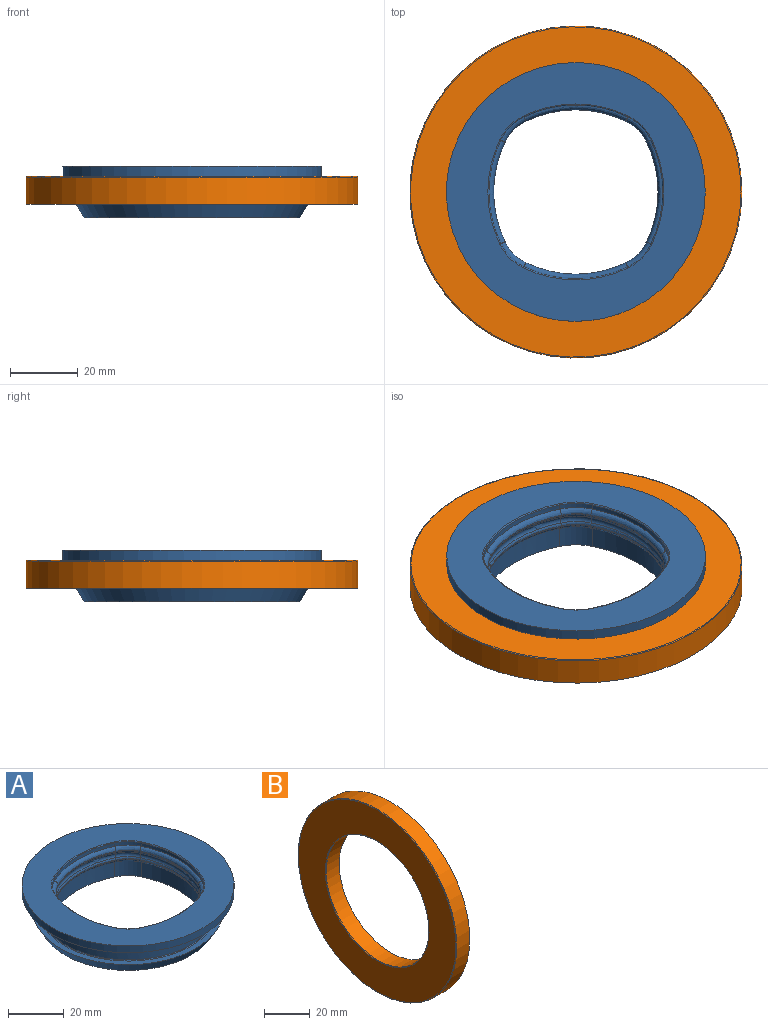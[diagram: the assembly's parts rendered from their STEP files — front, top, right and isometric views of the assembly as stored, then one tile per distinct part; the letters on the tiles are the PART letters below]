
ASSEMBLY  parts=2 mates=1
PART A: 89 faces, bbox 76.2x76.2x15.2 mm
  f0: cylinder r=38.1mm len=76.2mm, axis (0,0,1), area 717.5mm2, adj f2,f75
  f1: plane 63.5x63.5mm, normal (0,0,-1), area 997.1mm2, adj f19,f20,f21,f22,f23,f24,f25,f26
  f2: plane 76.2x76.2mm, normal (0,0,1), area 2340.6mm2, adj f0,f81,f82,f83,f84,f85,f86,f87
  f3: cylinder r=14.09mm len=6.8mm, axis (0,0,-1), area 14.5mm2, adj f4,f5,f16,f88
  f4: cylinder r=34.92mm len=30.56mm, axis (0,0,-1), area 46.7mm2, adj f3,f6,f17,f86
  f5: cylinder r=34.92mm len=30.56mm, axis (0,0,-1), area 46.7mm2, adj f3,f7,f15,f87
  f6: cylinder r=14.09mm len=6.8mm, axis (0,0,-1), area 14.5mm2, adj f4,f8,f18,f84
  f7: cylinder r=14.09mm len=6.8mm, axis (0,0,-1), area 14.5mm2, adj f5,f9,f14,f85
  f8: cylinder r=34.92mm len=30.56mm, axis (0,0,-1), area 46.7mm2, adj f6,f10,f11,f82
  f9: cylinder r=34.92mm len=30.56mm, axis (0,0,-1), area 46.7mm2, adj f7,f10,f13,f83
  f10: cylinder r=14.09mm len=6.8mm, axis (0,0,-1), area 14.5mm2, adj f8,f9,f12,f81
  f11: bspline ~30.7x5.32mm, area 63.4mm2, adj f8,f12,f18,f35
  f12: bspline ~7.41x7.41mm, area 19mm2, adj f10,f11,f13,f36
  f13: bspline ~30.7x5.32mm, area 63.4mm2, adj f9,f12,f14,f37
  f14: bspline ~7.41x7.41mm, area 19mm2, adj f7,f13,f15,f38
  f15: bspline ~30.7x5.32mm, area 63.4mm2, adj f5,f14,f16,f39
  f16: bspline ~7.41x7.41mm, area 19mm2, adj f3,f15,f17,f40
  f17: bspline ~30.7x5.32mm, area 63.4mm2, adj f4,f16,f18,f41
  f18: bspline ~7.41x7.41mm, area 19mm2, adj f6,f11,f17,f42
  f19: cylinder r=14.09mm len=6.86mm, axis (0,0,-1), area 67.3mm2, adj f1,f20,f21,f32
  f20: cylinder r=34.92mm len=30.56mm, axis (0,0,-1), area 216.9mm2, adj f1,f19,f22,f33
  f21: cylinder r=34.92mm len=30.56mm, axis (0,0,-1), area 216.9mm2, adj f1,f19,f23,f31
  f22: cylinder r=14.09mm len=6.86mm, axis (0,0,-1), area 67.3mm2, adj f1,f20,f24,f34
  f23: cylinder r=14.09mm len=6.86mm, axis (0,0,-1), area 67.3mm2, adj f1,f21,f25,f30
  f24: cylinder r=34.92mm len=30.56mm, axis (0,0,-1), area 216.9mm2, adj f1,f22,f26,f27
  f25: cylinder r=34.92mm len=30.56mm, axis (0,0,-1), area 216.9mm2, adj f1,f23,f26,f29
  f26: cylinder r=14.09mm len=6.86mm, axis (0,0,-1), area 67.3mm2, adj f1,f24,f25,f28
  f27: bspline ~30.7x5.32mm, area 63.4mm2, adj f24,f28,f34,f67
  f28: bspline ~7.91x7.91mm, area 19mm2, adj f26,f27,f29,f68
  f29: bspline ~30.7x5.32mm, area 63.4mm2, adj f25,f28,f30,f69
  f30: bspline ~7.91x7.91mm, area 19mm2, adj f23,f29,f31,f70
  f31: bspline ~30.7x5.32mm, area 63.4mm2, adj f21,f30,f32,f71
  f32: bspline ~7.91x7.91mm, area 19mm2, adj f19,f31,f33,f72
  f33: bspline ~30.7x5.32mm, area 63.4mm2, adj f20,f32,f34,f73
  f34: bspline ~7.91x7.91mm, area 19mm2, adj f22,f27,f33,f74
  f35: cylinder r=33.53mm len=29.36mm, axis (0,0,1), area 8.5mm2, adj f11,f36,f42,f56
  f36: cylinder r=12.7mm len=6.15mm, axis (0,0,1), area 2.5mm2, adj f12,f35,f37,f54
  f37: cylinder r=33.53mm len=29.36mm, axis (0,0,1), area 8.5mm2, adj f13,f36,f38,f52
  f38: cylinder r=12.7mm len=6.15mm, axis (0,0,1), area 2.5mm2, adj f14,f37,f39,f50
  f39: cylinder r=33.53mm len=29.36mm, axis (0,0,1), area 8.5mm2, adj f15,f38,f40,f48
  f40: cylinder r=12.7mm len=6.15mm, axis (0,0,1), area 2.5mm2, adj f16,f39,f41,f46
  f41: cylinder r=33.53mm len=29.36mm, axis (0,0,1), area 8.5mm2, adj f17,f40,f42,f44
  f42: cylinder r=12.7mm len=6.15mm, axis (0,0,1), area 2.5mm2, adj f18,f35,f41,f58
  f43: bspline ~29.65x3.71mm, area 26mm2, adj f45,f57,f65,f73
  f44: bspline ~29.65x3.71mm, area 26mm2, adj f41,f46,f58,f65
  f45: bspline ~7.74x7.74mm, area 7.6mm2, adj f43,f47,f66,f72
  f46: bspline ~6.45x6.45mm, area 7.6mm2, adj f40,f44,f48,f66
  f47: bspline ~29.65x3.71mm, area 26mm2, adj f45,f49,f64,f71
  f48: bspline ~29.65x3.71mm, area 26mm2, adj f39,f46,f50,f64
  f49: bspline ~7.74x7.74mm, area 7.6mm2, adj f47,f51,f62,f70
  f50: bspline ~6.45x6.45mm, area 7.6mm2, adj f38,f48,f52,f62
  f51: bspline ~29.65x3.71mm, area 26mm2, adj f49,f53,f60,f69
  f52: bspline ~29.65x3.71mm, area 26mm2, adj f37,f50,f54,f60
  f53: bspline ~7.74x7.74mm, area 7.6mm2, adj f51,f55,f59,f68
  f54: bspline ~6.45x6.45mm, area 7.6mm2, adj f36,f52,f56,f59
  f55: bspline ~29.65x3.71mm, area 26mm2, adj f53,f57,f61,f67
  f56: bspline ~29.65x3.71mm, area 26mm2, adj f35,f54,f58,f61
  f57: bspline ~7.74x7.74mm, area 7.6mm2, adj f43,f55,f63,f74
  f58: bspline ~6.45x6.45mm, area 7.6mm2, adj f42,f44,f56,f63
  f59: torus R=11.88mm, axis (0,0,-1), area 20.1mm2, adj f53,f54,f60,f61
  f60: torus R=32.7mm, axis (0,0,-1), area 66.9mm2, adj f51,f52,f59,f62
  f61: torus R=32.7mm, axis (0,0,-1), area 66.9mm2, adj f55,f56,f59,f63
  f62: torus R=11.88mm, axis (0,0,-1), area 20.1mm2, adj f49,f50,f60,f64
  f63: torus R=11.88mm, axis (0,0,-1), area 20.1mm2, adj f57,f58,f61,f65
  f64: torus R=32.7mm, axis (0,0,-1), area 66.9mm2, adj f47,f48,f62,f66
  f65: torus R=32.7mm, axis (0,0,-1), area 66.9mm2, adj f43,f44,f63,f66
  f66: torus R=11.88mm, axis (0,0,-1), area 20.1mm2, adj f45,f46,f64,f65
  f67: cylinder r=33.53mm len=29.36mm, axis (0,0,1), area 8.5mm2, adj f27,f55,f68,f74
  f68: cylinder r=12.7mm len=6.15mm, axis (0,0,1), area 2.5mm2, adj f28,f53,f67,f69
  f69: cylinder r=33.53mm len=29.36mm, axis (0,0,1), area 8.5mm2, adj f29,f51,f68,f70
  f70: cylinder r=12.7mm len=6.15mm, axis (0,0,1), area 2.5mm2, adj f30,f49,f69,f71
  f71: cylinder r=33.53mm len=29.36mm, axis (0,0,1), area 8.5mm2, adj f31,f47,f70,f72
  f72: cylinder r=12.7mm len=6.15mm, axis (0,0,1), area 2.5mm2, adj f32,f45,f71,f73
  f73: cylinder r=33.53mm len=29.36mm, axis (0,0,1), area 8.5mm2, adj f33,f43,f72,f74
  f74: cylinder r=12.7mm len=6.15mm, axis (0,0,1), area 2.5mm2, adj f34,f57,f67,f73
  f75: plane 76.2x76.2mm, normal (0,0,-1), area 1333.3mm2, adj f0,f79
  f76: cylinder r=31.75mm len=63.5mm, axis (0,0,1), area 1461.2mm2, adj f79,f80
  f77: plane 68.58x68.58mm, normal (0,0,1), area 466.8mm2, adj f78,f80
  f78: cone r=34.29mm half-angle=30.5deg, axis (0,0,1), area 1039.4mm2, adj f1,f77
  f79: torus R=32.05mm, axis (0,0,-1), area 94.3mm2, adj f75,f76
  f80: torus R=32.05mm, axis (0,0,1), area 94.3mm2, adj f76,f77
  f81: torus R=14.39mm, axis (0,0,1), area 4.7mm2, adj f2,f10,f82,f83
  f82: torus R=35.22mm, axis (0,0,1), area 15mm2, adj f2,f8,f81,f84
  f83: torus R=35.22mm, axis (0,0,1), area 15mm2, adj f2,f9,f81,f85
  f84: torus R=14.39mm, axis (0,0,1), area 4.7mm2, adj f2,f6,f82,f86
  f85: torus R=14.39mm, axis (0,0,1), area 4.7mm2, adj f2,f7,f83,f87
  f86: torus R=35.22mm, axis (0,0,1), area 15mm2, adj f2,f4,f84,f88
  f87: torus R=35.22mm, axis (0,0,1), area 15mm2, adj f2,f5,f85,f88
  f88: torus R=14.39mm, axis (0,0,1), area 4.7mm2, adj f2,f3,f86,f87
PART B: 12 faces, bbox 8.3x105.8x105.8 mm
  f0: cylinder r=48.13mm len=96.27mm, axis (-1,0,0), area 2189.3mm2, adj f1,f11
  f1: plane 97.79x97.79mm, normal (1,0,0), area 232.3mm2, adj f0,f2
  f2: cylinder r=48.9mm len=97.79mm, axis (-1,0,0), area 2458mm2, adj f1,f8
  f3: plane 97.28x97.28mm, normal (-1,0,0), area 4215mm2, adj f8,f9
  f4: cylinder r=31.75mm len=63.5mm, axis (-1,0,0), area 1596.1mm2, adj f5,f9
  f5: plane 65.02x65.02mm, normal (1,0,0), area 153.8mm2, adj f4,f6
  f6: cylinder r=32.51mm len=65.02mm, axis (-1,0,0), area 1478.8mm2, adj f5,f10
  f7: plane 95.76x95.76mm, normal (1,0,0), area 3828.9mm2, adj f10,f11
  f8: torus R=48.64mm, axis (-1,0,0), area 122.3mm2, adj f2,f3
  f9: torus R=32mm, axis (-1,0,0), area 79.8mm2, adj f3,f4
  f10: torus R=32.77mm, axis (1,0,0), area 81.7mm2, adj f6,f7
  f11: torus R=47.88mm, axis (1,0,0), area 120.4mm2, adj f0,f7
PLACE A at identity
PLACE B rot(axis=(0,1,0),90deg) t=(0,0,-3)mm
MATE fastened B.f0 <-> A.f0  axis (0,0,1) through (0,0,-3)mm
